# Revit family: IS_ConnectSpace_Multiproduct_BIM_FR_E1290;E1291
name_source: partatom
category: Plumbing Fixtures
revit_build: Autodesk Revit MEP 2016 (Build: 20161004_0715(x64)
units: mm (PartAtom-declared; Revit-internal decimal feet)

## family parameters
Cut with Voids When Loaded = Yes
Host = Face
OmniClass Number = 23.45.05.21.11.11
OmniClass Title = Water Operated Water Closets
Part Type = Normal
Room Calculation Point = No
Round Connector Dimension = Use Diameter
Shared = No

## types (2) — shared parameters
Accessoires = www.idealspec.fr
Bim-NomDuProjet = ISI_IdealStandard_ConnectSpace_E1290_E1291
Conformité = NF
ConseilsDInstallation = 0
Couleur = Blanc
DateDeCréation = 43351
DescripciónUniclass2015 = WCSEATS
Dimensions = 45 x 366 x 395 mm
Espace = Interne
Finition = Blanc
Forme = Complexe
Hauteur = 45 mm  [stored 0.147638 ft]
IfcExportAs = IfcSanitaryTerminalType
IfcExportType = WCSEATS
IfcExportaComo = IfcSanitaryTerminalType
InformationsProduit = www.idealspec.fr
Largeur = 366 mm
Longueur = 395 mm  [stored 1.29593 ft]
Marque = Ideal Standard
Matériel = Plastique
PoidsNet = 0
Raccordement = Plomberie
ReferenciaUniclass2015 = Pr_40_20_93_95
Révision = 1
URL = www.idealspec.fr
Uniclass2015Code = Pr_40_20_93_95
Uniclass2015Title = WC seats and covers
UnitéDeMesure = Millimètres
UnitéDeTemps = An
UnitéMonétaire = €
UrlDuFabricant = www.idealspec.fr
zero-valued in all types: Cost, CoûtDeRemplacement, Default Elevation, Profondeur

## per-type parameters (varying)
| type | Caractéristiques | CodeBarre | Description | Model | NombreDeObjetoBim |
| E129001 - Asiento y tapa Connect Space, caída normal, blanco | Connect Space Abattant Recouvrant Blanc | 5017830447986 | Connect Space Abattant Recouvrant Blanc | E129001 | ISI_IdealStandard_WcSeatsAndCovers_Connect_E129001 |
| E129101 - Asiento y tapa Connect Space, caída amortiguada, blanco | Connect Space Abattant Frein De Chute Blanc | 5017830447993 | Connect Space Abattant Frein De Chute Blanc | E129101 | ISI_IdealStandard_WcSeatsAndCovers_Connect_E129101 |

note: [stored X ft] marks values corroborated as IEEE doubles in the binary element streams (Revit-internal decimal feet)

## geometry (parser evidence)
native form markers: Blend x4, Sweep x1
no freeform markers — native parametric forms only
